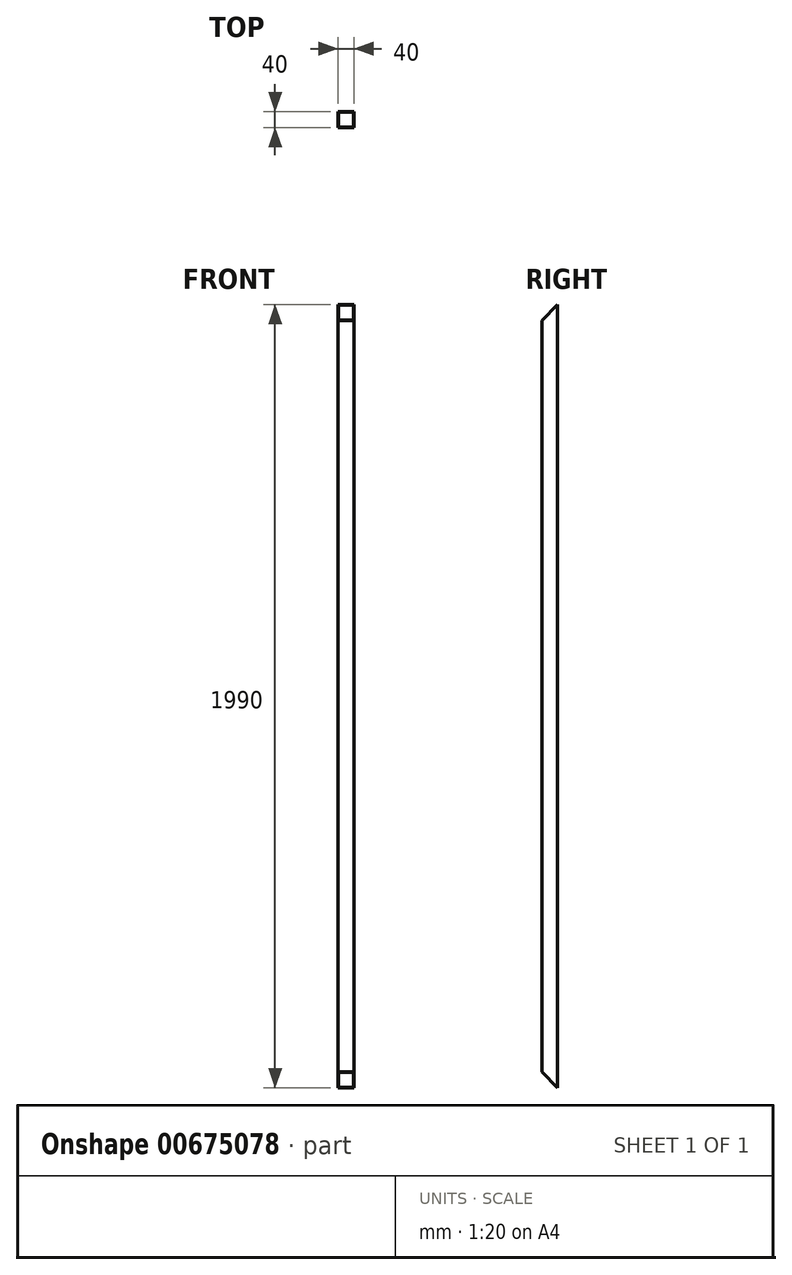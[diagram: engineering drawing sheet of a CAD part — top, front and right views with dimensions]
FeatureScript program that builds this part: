
annotation { "Feature Type Name" : "Feature", "Feature Type Description" : "" }
export const myFeature = defineFeature(function(context is Context, id is Id, definition is map)
    precondition{}
    {
        {
            var Q0;
            Q0=qCreatedBy(makeId("Top.planeOp"),FACE);
            var sketch = newSketch(context, id + "F0", { "sketchPlane" : qUnion([Q0])});
            skLineSegment(sketch, "E0.bottom", {"start": v(19, 19) * mm, "end": v(-19, 19) * mm});
            skLineSegment(sketch, "E0.top", {"start": v(19, -19) * mm, "end": v(-19, -19) * mm});
            skLineSegment(sketch, "E0.left", {"start": v(19, 19) * mm, "end": v(19, -19) * mm});
            skLineSegment(sketch, "E0.right", {"start": v(-19, 19) * mm, "end": v(-19, -19) * mm});
            skPoint(sketch, "E0.middle", {"position": v(0, 0) * mm});
            skLineSegment(sketch, "E1.bottom", {"start": v(20, 20) * mm, "end": v(-20, 20) * mm});
            skLineSegment(sketch, "E1.top", {"start": v(20, -20) * mm, "end": v(-20, -20) * mm});
            skLineSegment(sketch, "E1.left", {"start": v(20, 20) * mm, "end": v(20, -20) * mm});
            skLineSegment(sketch, "E1.right", {"start": v(-20, 20) * mm, "end": v(-20, -20) * mm});
            skSolve(sketch);
        }
        {
            var Q0;
            Q0=makeQuery(id+"F0.imprint","IMPRINT",FACE,{"disambiguationData":[TD([[makeQuery(id+"F0.imprint","IMPRINT",EDGE,{"derivedFrom":sQuery(id+"F0.wireOp",EDGE,"E0.bottom")}),-1.0]])]});
            extrude(context, id + "F1", {"entities" : qUnion([Q0]), "depth" : 1990 * mm, "offsetDistance" : 25 * mm});
        }
        {
            var Q0;
            Q0=makeQuery(id+"F1.opExtrude","SWEPT_FACE",FACE,{"disambiguationData":[OSD([sQuery(id+"F0.wireOp",EDGE,"E1.left")])]});
            var sketch = newSketch(context, id + "F2", { "sketchPlane" : qUnion([Q0])});
            skLineSegment(sketch, "E2", {"start": v(20, 1990) * mm, "end": v(-20, 1950) * mm});
            skSolve(sketch);
        }
        {
            var Q0;
            {var subQ0=sQuery(id+"F2.wireOp",EDGE,"E2");Q0=makeQuery(id+"F2.imprint","IMPRINT",FACE,{"disambiguationData":[TD([[makeQuery(id+"F2.imprint","IMPRINT",EDGE,{"derivedFrom":subQ0}),-1.0]])]});}
            extrude(context, id + "F3", {"entities" : qUnion([Q0]), "operationType" : NewBodyOperationType.REMOVE, "oppositeDirection" : true, "depth" : 100 * mm, "offsetDistance" : 25 * mm});
        }
        {
            var Q0;
            Q0=makeQuery(id+"F1.opExtrude","SWEPT_FACE",FACE,{"disambiguationData":[OSD([sQuery(id+"F0.wireOp",EDGE,"E1.left")])]});
            var sketch = newSketch(context, id + "F4", { "sketchPlane" : qUnion([Q0])});
            skLineSegment(sketch, "E3", {"start": v(20, 0) * mm, "end": v(-20, 40) * mm});
            skSolve(sketch);
        }
        {
            var Q0;
            {var subQ0=sQuery(id+"F4.wireOp",EDGE,"E3");Q0=makeQuery(id+"F4.imprint","IMPRINT",FACE,{"disambiguationData":[TD([[makeQuery(id+"F4.imprint","IMPRINT",EDGE,{"derivedFrom":subQ0}),1.0]])]});}
            extrude(context, id + "F5", {"entities" : qUnion([Q0]), "operationType" : NewBodyOperationType.REMOVE, "oppositeDirection" : true, "depth" : 99 * mm, "offsetDistance" : 25 * mm});
        }
    });
